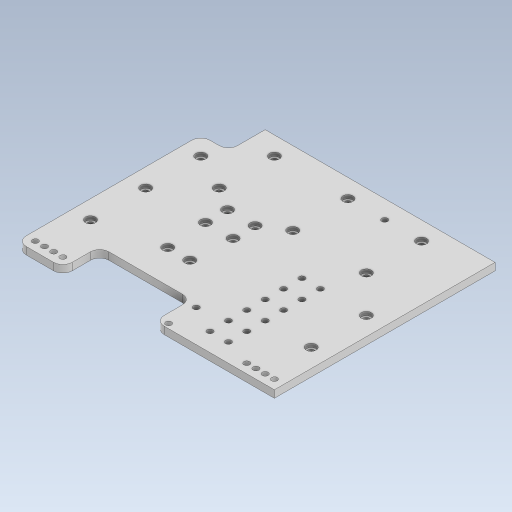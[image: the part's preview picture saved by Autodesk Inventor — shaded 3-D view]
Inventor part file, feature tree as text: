
AUTODESK INVENTOR PART (.ipt)
format: ipt  version: 2023.5 (Build 275446000, 446)  size: 546,816 bytes
history: native  units: in
note: dims shown in document units (in); Inventor stores cm internally (conversion verified against a paired STEP export)
features: extrude x2, sketch x1, fillet x1
ambient origin geometry x8: Origin, YZ Plane, XZ Plane, XY Plane, X Axis, Y Axis, Z Axis, Center Point
bodies: Solid1 (feature_tree)
feature tree (4):
  sketch  "Sketch1"  dims[d0=5.5118in d1=4.7244in d2=1.9685in d3=0.7874in d4=0.9843in d5=0.126in d6=0.1969in d7=0.1969in d8=0.126in d9=0.1969in d10=0.126in d11=0.1969in d12=0.126in d13=0.1969in d14=0.126in d15=0.3937in d16=1.1811in d17=0.126in d18=0.2165in d19=0.2165in d20=0.126in d22=0.2165in d23=0.126in d24=0.2165in d28=0.126in d30=0.2165in d34=0.126in d37=0.2165in d38=0.1575in d39=0.0in d40=0.0787in d41=0.0in d42=1.1811in d43=0.3937in d44=0.3937in d46=0.3937in d47=0.126in d48=0.1969in d49=0.0984in d50=0.126in d51=0.5906in d52=0.126in d53=0.126in d54=0.3937in d55=0.126in d56=0.3937in d57=0.126in d58=0.7874in d59=0.3937in d60=0.3937in d61=0.126in d62=0.3937in d63=0.126in d64=0.3937in d65=0.126in d66=0.126in d67=0.126in d68=0.3937in d69=0.126in d70=0.3937in d71=0.126in d72=0.126in d73=0.1299in d74=0.2165in d76=0.1299in d77=0.2165in d78=1.1811in d79=1.1811in d80=0.5906in d81=0.7874in d82=0.1969in d83=0.126in d84=0.7874in]
  extrude  "Extrusion1"  Depth=4.7244in
  extrude  "Extrusion2"  Depth=1.9685in
  fillet  "Fillet1"  Radius=0.7874in
